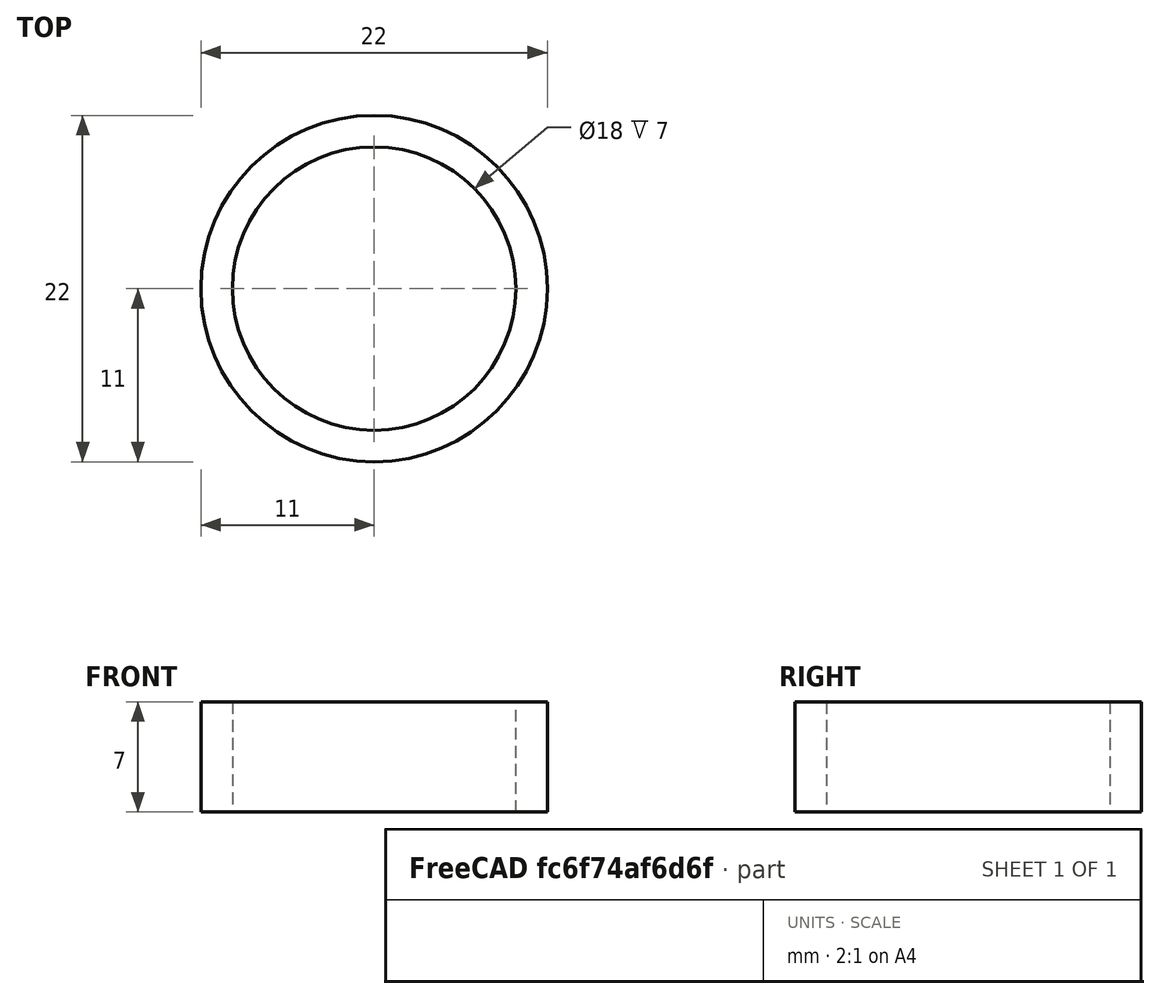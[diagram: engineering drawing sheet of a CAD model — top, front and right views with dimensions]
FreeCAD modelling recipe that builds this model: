
FCSTD DOCUMENT  (FreeCAD 0.19R24276 (Git))
Label: Ring_22x18
License: All rights reserved
LicenseURL: http://en.wikipedia.org/wiki/All_rights_reserved
objects: Sketcher::SketchObject×1, PartDesign::Pad×1, PartDesign::Body×1
note: 4 computed .brp shape members not serialized (recipe doc carries the construction recipe); baked Part::Feature solids carry a one-line shape summary decoded from their .brp

FEATURE [Sketcher::SketchObject] Sketch
  FullyConstrained = true
  MapMode = 5
  Support = -> [XY_Plane]
  sketch-geometry (2):
    g0: Circle CenterX=0 CenterY=0 CenterZ=0 NormalX=0 NormalY=0 NormalZ=1 AngleXU=0 Radius=9
    g1: Circle CenterX=0 CenterY=0 CenterZ=0 NormalX=0 NormalY=0 NormalZ=1 AngleXU=0 Radius=11
  constraints (4):
    c: Coincident(g1,g0)
    c: Diameter(g1) = 22
    c: Diameter(g0) = 18
    c: Coincident(g0,g-1)
FEATURE [PartDesign::Pad] Pad
  Direction = (1,1,1)
  Length = 7
  Length2 = 100
  Profile = -> Sketch
  Type = 0
FEATURE [PartDesign::Body] Body
  Group = -> [Sketch,Pad]
  Origin = -> Origin
  Tip = -> Pad
